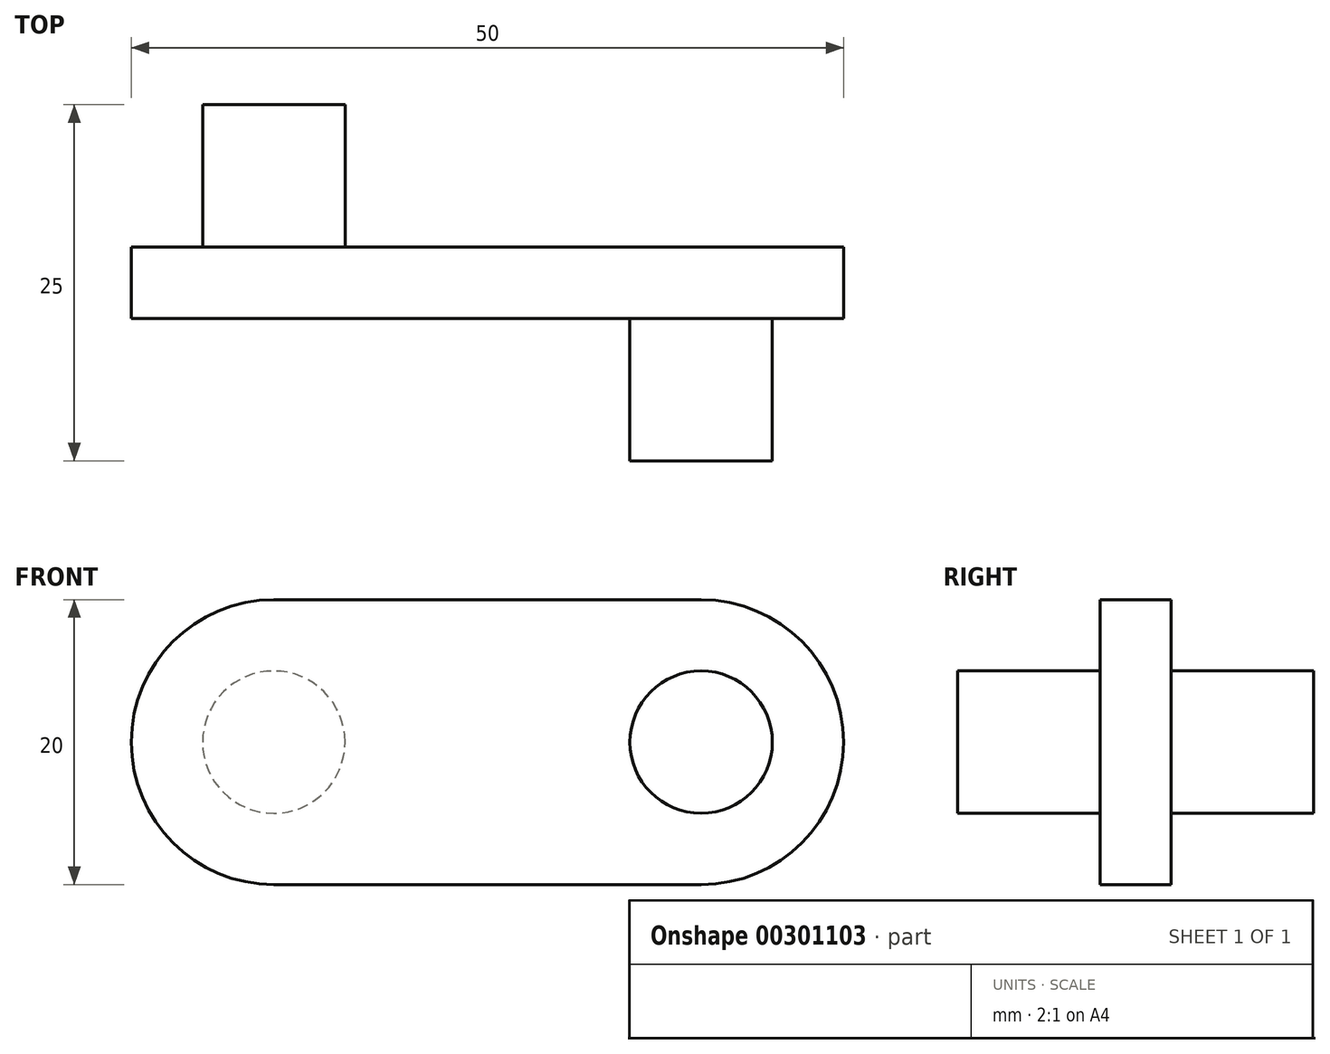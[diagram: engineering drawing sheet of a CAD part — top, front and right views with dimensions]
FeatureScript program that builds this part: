
annotation { "Feature Type Name" : "Feature", "Feature Type Description" : "" }
export const myFeature = defineFeature(function(context is Context, id is Id, definition is map)
    precondition{}
    {
        {
            var Q0;
            Q0=qCreatedBy(makeId("Front.planeOp"),FACE);
            var sketch = newSketch(context, id + "F0", { "sketchPlane" : qUnion([Q0])});
            skLineSegment(sketch, "E0.bottom", {"start": v(10, 0) * mm, "end": v(40, 0) * mm});
            skLineSegment(sketch, "E0.top", {"start": v(10, 20) * mm, "end": v(40, 20) * mm});
            skLineSegment(sketch, "E0.left", {"start": v(0, 10) * mm, "end": v(0, 10) * mm});
            skLineSegment(sketch, "E0.right", {"start": v(50, 10) * mm, "end": v(50, 10) * mm});
            skPoint(sketch, "E1.visualSharp", {"position": v(0, 20) * mm});
            skArc(sketch, "E1.filletArc", {"start": v(10, 20) * mm, "mid": v(2.93, 17.07) * mm, "end": v(0, 10) * mm});
            skPoint(sketch, "E2.visualSharp", {"position": v(0, 0) * mm});
            skArc(sketch, "E2.filletArc", {"start": v(0, 10) * mm, "mid": v(2.93, 2.93) * mm, "end": v(10, 0) * mm});
            skPoint(sketch, "E3.visualSharp", {"position": v(50, 0) * mm});
            skArc(sketch, "E3.filletArc", {"start": v(40, 0) * mm, "mid": v(47.07, 2.93) * mm, "end": v(50, 10) * mm});
            skPoint(sketch, "E4.visualSharp", {"position": v(50, 20) * mm});
            skArc(sketch, "E4.filletArc", {"start": v(50, 10) * mm, "mid": v(47.07, 17.07) * mm, "end": v(40, 20) * mm});
            skSolve(sketch);
        }
        {
            var Q0;
            Q0 = qSketchRegion(id + "F0", true);
            extrude(context, id + "F1", {"entities" : qUnion([Q0]), "oppositeDirection" : true, "depth" : 5 * mm});
        }
        {
            var Q0;
            Q0=makeQuery(id+"F1.opExtrude","CAP_FACE",FACE,{"disambiguationData":[OSD([sQuery(id+"F0.wireOp",EDGE,"E0.bottom"),sQuery(id+"F0.wireOp",EDGE,"E0.top"),sQuery(id+"F0.wireOp",EDGE,"E1.filletArc"),sQuery(id+"F0.wireOp",EDGE,"E2.filletArc"),sQuery(id+"F0.wireOp",EDGE,"E3.filletArc"),sQuery(id+"F0.wireOp",EDGE,"E4.filletArc")])],"isStart":true});
            var sketch = newSketch(context, id + "F2", { "sketchPlane" : qUnion([Q0])});
            skCircle(sketch, "E5", {"center": v(40, 10) * mm, "radius": 5 * mm});
            skSolve(sketch);
        }
        {
            var Q0;
            Q0 = qSketchRegion(id + "F2", true);
            extrude(context, id + "F3", {"entities" : qUnion([Q0]), "operationType" : NewBodyOperationType.ADD, "depth" : 10 * mm});
        }
        {
            var Q0;
            Q0=makeQuery(id+"F1.opExtrude","CAP_FACE",FACE,{"disambiguationData":[OSD([sQuery(id+"F0.wireOp",EDGE,"E0.bottom"),sQuery(id+"F0.wireOp",EDGE,"E0.top"),sQuery(id+"F0.wireOp",EDGE,"E1.filletArc"),sQuery(id+"F0.wireOp",EDGE,"E2.filletArc"),sQuery(id+"F0.wireOp",EDGE,"E3.filletArc"),sQuery(id+"F0.wireOp",EDGE,"E4.filletArc")])],"isStart":false});
            var sketch = newSketch(context, id + "F4", { "sketchPlane" : qUnion([Q0])});
            skCircle(sketch, "E6", {"center": v(-10, 10) * mm, "radius": 5 * mm});
            skSolve(sketch);
        }
        {
            var Q0;
            Q0 = qSketchRegion(id + "F4", true);
            extrude(context, id + "F5", {"entities" : qUnion([Q0]), "operationType" : NewBodyOperationType.ADD, "depth" : 10 * mm});
        }
    });
